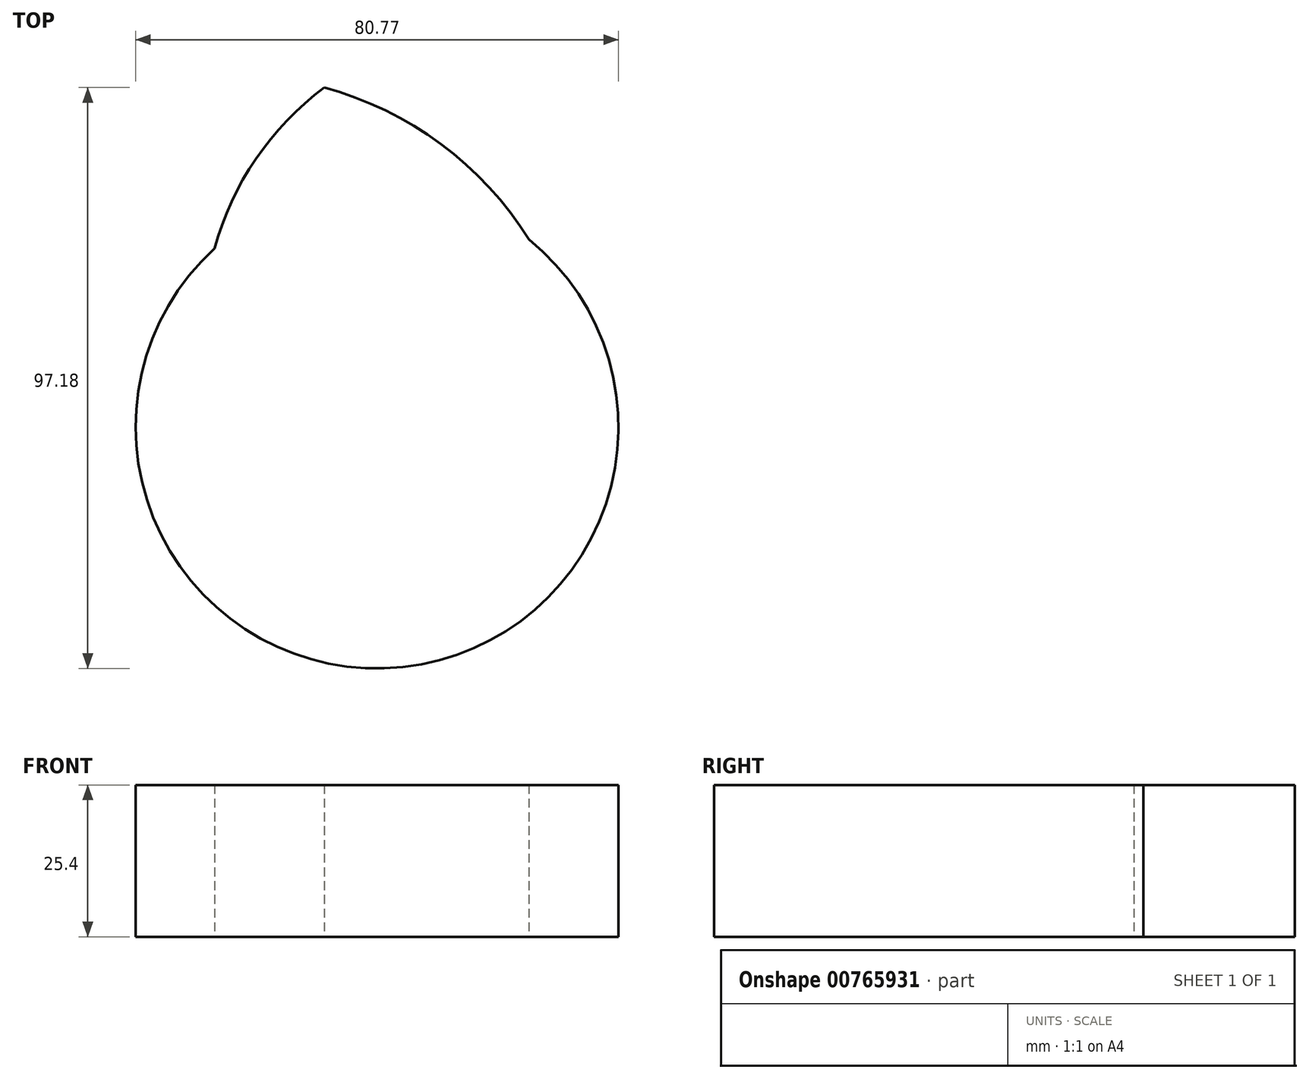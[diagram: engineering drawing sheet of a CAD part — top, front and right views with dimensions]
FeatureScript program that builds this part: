
annotation { "Feature Type Name" : "Feature", "Feature Type Description" : "" }
export const myFeature = defineFeature(function(context is Context, id is Id, definition is map)
    precondition{}
    {
        {
            var Q0;
            Q0=qCreatedBy(makeId("Top.planeOp"),FACE);
            var sketch = newSketch(context, id + "F0", { "sketchPlane" : qUnion([Q0])});
            skLineSegment(sketch, "E0.bottom", {"start": v(-71, 6.1) * mm, "end": v(-4.43, 6.1) * mm});
            skLineSegment(sketch, "E0.top", {"start": v(-71, 20.77) * mm, "end": v(-4.43, 20.77) * mm});
            skLineSegment(sketch, "E0.left", {"start": v(-71, 6.1) * mm, "end": v(-71, 20.77) * mm});
            skLineSegment(sketch, "E0.right", {"start": v(-4.43, 6.1) * mm, "end": v(-4.43, 20.77) * mm});
            skLineSegment(sketch, "E1.bottom", {"start": v(-55.12, 6.1) * mm, "end": v(-19.7, 6.1) * mm});
            skLineSegment(sketch, "E1.top", {"start": v(-55.12, -20.61) * mm, "end": v(-19.7, -20.61) * mm});
            skLineSegment(sketch, "E1.left", {"start": v(-55.12, 6.1) * mm, "end": v(-55.12, -20.61) * mm});
            skLineSegment(sketch, "E1.right", {"start": v(-19.7, 6.1) * mm, "end": v(-19.7, -20.61) * mm});
            skLineSegment(sketch, "E2.bottom", {"start": v(-55.12, -20.61) * mm, "end": v(-70.09, -20.61) * mm});
            skLineSegment(sketch, "E2.top", {"start": v(-55.12, -20.61) * mm, "end": v(-70.09, -20.61) * mm});
            skLineSegment(sketch, "E2.left", {"start": v(-55.12, -20.61) * mm, "end": v(-55.12, -20.61) * mm});
            skLineSegment(sketch, "E2.right", {"start": v(-70.09, -20.61) * mm, "end": v(-70.09, -20.61) * mm});
            skLineSegment(sketch, "E3.bottom", {"start": v(-70.09, -20.61) * mm, "end": v(-4.12, -20.61) * mm});
            skLineSegment(sketch, "E3.top", {"start": v(-70.09, -36.5) * mm, "end": v(-4.12, -36.5) * mm});
            skLineSegment(sketch, "E3.left", {"start": v(-70.09, -20.61) * mm, "end": v(-70.09, -36.5) * mm});
            skLineSegment(sketch, "E3.right", {"start": v(-4.12, -20.61) * mm, "end": v(-4.12, -36.5) * mm});
            skCircle(sketch, "E4", {"center": v(-37.1, -5.04) * mm, "radius": 40.38 * mm});
            skArc(sketch, "E5", {"start": v(-45.96, 51.76) * mm, "mid": v(-57.38, 39.82) * mm, "end": v(-64.3, 24.82) * mm});
            skArc(sketch, "E6", {"start": v(-11.72, 26.37) * mm, "mid": v(-26.44, 42.3) * mm, "end": v(-45.96, 51.76) * mm});
            skSolve(sketch);
        }
        {
            var Q0;
            Q0=makeQuery(id+"F0.imprint","IMPRINT",FACE,{"disambiguationData":[TD([[makeQuery(id+"F0.imprint","IMPRINT",EDGE,{"derivedFrom":sQuery(id+"F0.wireOp",EDGE,"E1.top")}),1.0]])]});
            var Q1;
            Q1=makeQuery(id+"F0.imprint","IMPRINT",FACE,{"disambiguationData":[TD([[makeQuery(id+"F0.imprint","IMPRINT",EDGE,{"derivedFrom":sQuery(id+"F0.wireOp",EDGE,"E1.top")}),-1.0]])]});
            var Q2;
            {var subQ0=sQuery(id+"F0.wireOp",EDGE,"E4");var subQ1=sQuery(id+"F0.wireOp",EDGE,"E3.top");var subQ2=makeQuery(id+"F0.imprint","INTERSECT",VERTEX,{"disambiguationData":[OD(0.0)],"derivedFrom":[subQ1,subQ0]});Q2=makeQuery(id+"F0.imprint","IMPRINT",FACE,{"disambiguationData":[TD([[makeQuery(id+"F0.imprint","IMPRINT",EDGE,{"disambiguationData":[TD([[subQ2,-1.0]])],"derivedFrom":subQ1}),-1.0]])]});}
            var Q3;
            {var subQ6=sQuery(id+"F0.wireOp",EDGE,"E1.right");Q3=makeQuery(id+"F0.imprint","IMPRINT",FACE,{"disambiguationData":[TD([[makeQuery(id+"F0.imprint","IMPRINT",EDGE,{"derivedFrom":subQ6}),1.0]])]});}
            var Q4;
            {var subQ0=sQuery(id+"F0.wireOp",EDGE,"E5");Q4=makeQuery(id+"F0.imprint","IMPRINT",FACE,{"disambiguationData":[TD([[makeQuery(id+"F0.imprint","IMPRINT",EDGE,{"derivedFrom":subQ0}),1.0]])]});}
            var Q5;
            {var subQ5=sQuery(id+"F0.wireOp",EDGE,"E0.bottom");var subQ8=makeQuery(id+"F0.imprint","INTERSECT",VERTEX,{"derivedFrom":[subQ5,sQuery(id+"F0.wireOp",EDGE,"E1.left")]});Q5=makeQuery(id+"F0.imprint","IMPRINT",FACE,{"disambiguationData":[TD([[makeQuery(id+"F0.imprint","IMPRINT",EDGE,{"disambiguationData":[TD([[subQ8,-1.0]])],"derivedFrom":subQ5}),1.0]])]});}
            var Q6;
            {var subQ0=sQuery(id+"F0.wireOp",EDGE,"E4");var subQ1=sQuery(id+"F0.wireOp",EDGE,"E0.top");var subQ2=makeQuery(id+"F0.imprint","INTERSECT",VERTEX,{"disambiguationData":[OD(0.0)],"derivedFrom":[subQ1,subQ0]});Q6=makeQuery(id+"F0.imprint","IMPRINT",FACE,{"disambiguationData":[TD([[makeQuery(id+"F0.imprint","IMPRINT",EDGE,{"disambiguationData":[TD([[subQ2,-1.0]])],"derivedFrom":subQ1}),1.0]])]});}
            var Q7;
            {var subQ1=sQuery(id+"F0.wireOp",EDGE,"E1.left");Q7=makeQuery(id+"F0.imprint","IMPRINT",FACE,{"disambiguationData":[TD([[makeQuery(id+"F0.imprint","IMPRINT",EDGE,{"derivedFrom":subQ1}),-1.0]])]});}
            extrude(context, id + "F1", {"entities" : qUnion([Q0, Q1, Q2, Q3, Q4, Q5, Q6, Q7]), "depth" : 25.4 * mm, "offsetDistance" : 25.4 * mm});
        }
    });
